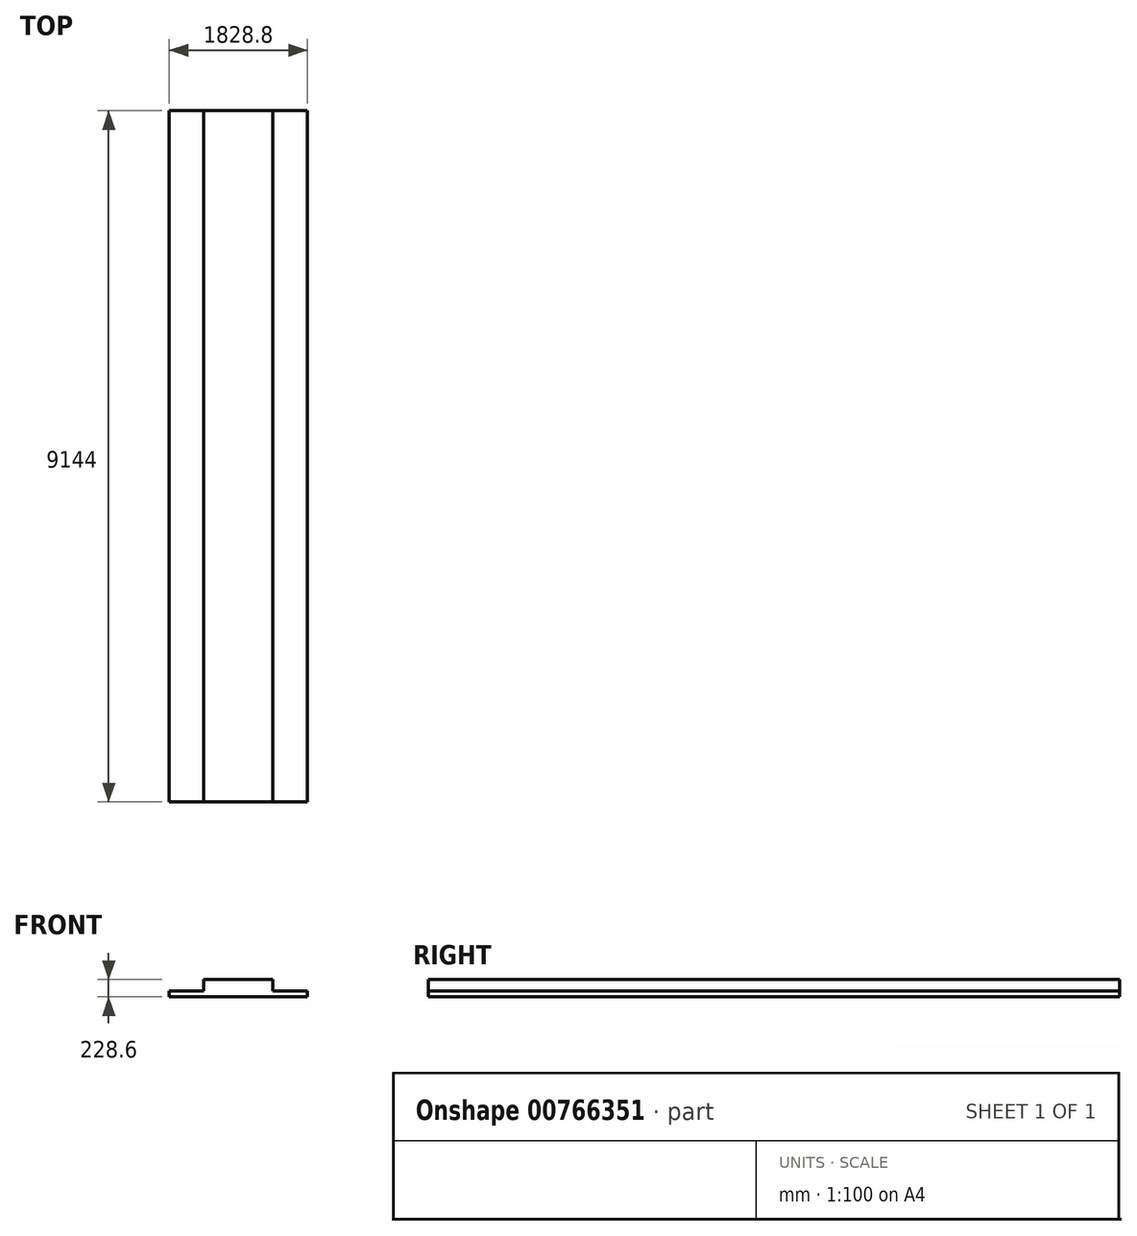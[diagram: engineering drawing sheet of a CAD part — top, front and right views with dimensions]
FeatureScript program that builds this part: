
annotation { "Feature Type Name" : "Feature", "Feature Type Description" : "" }
export const myFeature = defineFeature(function(context is Context, id is Id, definition is map)
    precondition{}
    {
        {
            var Q0;
            Q0=qCreatedBy(makeId("Front.planeOp"),FACE);
            var sketch = newSketch(context, id + "F0", { "sketchPlane" : qUnion([Q0])});
            skLineSegment(sketch, "E0.bottom", {"start": v(0, 0) * mm, "end": v(1828.8, 0) * mm});
            skLineSegment(sketch, "E0.left", {"start": v(0, 0) * mm, "end": v(0, 152.4) * mm});
            skLineSegment(sketch, "E0.right", {"start": v(1828.8, 0) * mm, "end": v(1828.8, 152.4) * mm});
            skLineSegment(sketch, "E1", {"start": v(1828.8, 0) * mm, "end": v(1828.8, -76.2) * mm});
            skLineSegment(sketch, "E2.top", {"start": v(0, -76.2) * mm, "end": v(1828.8, -76.2) * mm});
            skLineSegment(sketch, "E2.left", {"start": v(0, 0) * mm, "end": v(0, -76.2) * mm});
            skLineSegment(sketch, "E3", {"start": v(0, 76.2) * mm, "end": v(1828.8, 76.2) * mm});
            skLineSegment(sketch, "E4", {"start": v(914.4, 76.2) * mm, "end": v(1828.8, 76.2) * mm});
            skLineSegment(sketch, "E5", {"start": v(1371.6, 152.4) * mm, "end": v(1371.6, 0) * mm});
            skLineSegment(sketch, "E6", {"start": v(0, 152.4) * mm, "end": v(914.4, 152.4) * mm});
            skLineSegment(sketch, "E7", {"start": v(457.2, 152.4) * mm, "end": v(457.2, 0) * mm});
            skLineSegment(sketch, "E8", {"start": v(914.4, 152.4) * mm, "end": v(762, 152.4) * mm});
            skLineSegment(sketch, "E9", {"start": v(762, 152.4) * mm, "end": v(914.4, 152.4) * mm});
            skLineSegment(sketch, "E10", {"start": v(914.4, 152.4) * mm, "end": v(804.53, 152.4) * mm});
            skLineSegment(sketch, "E11", {"start": v(804.53, 152.4) * mm, "end": v(914.4, 152.4) * mm});
            skLineSegment(sketch, "E12", {"start": v(914.4, 152.4) * mm, "end": v(1066.8, 152.4) * mm});
            skLineSegment(sketch, "E13", {"start": v(1066.8, 152.4) * mm, "end": v(914.4, 152.4) * mm});
            skLineSegment(sketch, "E14", {"start": v(914.4, 152.4) * mm, "end": v(1828.8, 152.4) * mm});
            skLineSegment(sketch, "E15", {"start": v(762, 152.4) * mm, "end": v(762, 76.2) * mm});
            skLineSegment(sketch, "E16", {"start": v(762, 76.2) * mm, "end": v(457.2, 76.2) * mm});
            skLineSegment(sketch, "E17", {"start": v(457.2, 76.2) * mm, "end": v(457.2, 0) * mm});
            skLineSegment(sketch, "E18", {"start": v(1371.6, 0) * mm, "end": v(1371.6, 76.2) * mm});
            skLineSegment(sketch, "E19", {"start": v(1371.6, 76.2) * mm, "end": v(1066.8, 76.2) * mm});
            skLineSegment(sketch, "E20", {"start": v(1066.8, 76.2) * mm, "end": v(1066.8, 152.4) * mm});
            skLineSegment(sketch, "E21.bottom", {"start": v(762, 152.4) * mm, "end": v(1066.8, 152.4) * mm});
            skLineSegment(sketch, "E21.top", {"start": v(762, 76.2) * mm, "end": v(1066.8, 76.2) * mm});
            skLineSegment(sketch, "E21.right", {"start": v(1066.8, 152.4) * mm, "end": v(1066.8, 76.2) * mm});
            skLineSegment(sketch, "E22.bottom", {"start": v(457.2, 76.2) * mm, "end": v(1371.6, 76.2) * mm});
            skLineSegment(sketch, "E22.top", {"start": v(457.2, 0) * mm, "end": v(1371.6, 0) * mm});
            skLineSegment(sketch, "E22.right", {"start": v(1371.6, 76.2) * mm, "end": v(1371.6, 0) * mm});
            skSolve(sketch);
        }
        {
            var Q0;
            {var subQ2=sQuery(id+"F0.wireOp",EDGE,"E7");Q0=makeQuery(id+"F0.imprint","IMPRINT",FACE,{"disambiguationData":[TD([[makeQuery(id+"F0.imprint","IMPRINT",EDGE,{"derivedFrom":subQ2}),1.0]])]});}
            var Q1;
            {var subQ3=sQuery(id+"F0.wireOp",EDGE,"E3");Q1=makeQuery(id+"F0.imprint","IMPRINT",FACE,{"disambiguationData":[TD([[makeQuery(id+"F0.imprint","IMPRINT",EDGE,{"derivedFrom":subQ3}),1.0]])]});}
            var Q2;
            {var subQ3=sQuery(id+"F0.wireOp",EDGE,"E3");Q2=makeQuery(id+"F0.imprint","IMPRINT",FACE,{"disambiguationData":[TD([[makeQuery(id+"F0.imprint","IMPRINT",EDGE,{"derivedFrom":subQ3}),-1.0]])]});}
            var Q3;
            Q3=makeQuery(id+"F0.imprint","IMPRINT",FACE,{"disambiguationData":[TD([[makeQuery(id+"F0.imprint","IMPRINT",EDGE,{"derivedFrom":sQuery(id+"F0.wireOp",EDGE,"E2.top")}),1.0]])]});
            var Q4;
            {var subQ3=sQuery(id+"F0.wireOp",EDGE,"E4");Q4=makeQuery(id+"F0.imprint","IMPRINT",FACE,{"disambiguationData":[TD([[makeQuery(id+"F0.imprint","IMPRINT",EDGE,{"derivedFrom":subQ3}),-1.0]])]});}
            var Q5;
            {var subQ3=sQuery(id+"F0.wireOp",EDGE,"E4");Q5=makeQuery(id+"F0.imprint","IMPRINT",FACE,{"disambiguationData":[TD([[makeQuery(id+"F0.imprint","IMPRINT",EDGE,{"derivedFrom":subQ3}),1.0]])]});}
            var Q6;
            {var subQ0=sQuery(id+"F0.wireOp",EDGE,"E5");Q6=makeQuery(id+"F0.imprint","IMPRINT",FACE,{"disambiguationData":[TD([[makeQuery(id+"F0.imprint","IMPRINT",EDGE,{"derivedFrom":subQ0}),-1.0]])]});}
            extrude(context, id + "F1", {"entities" : qUnion([Q0, Q1, Q2, Q3, Q4, Q5, Q6]), "depth" : 9144 * mm, "offsetDistance" : 30.48 * mm});
        }
    });
